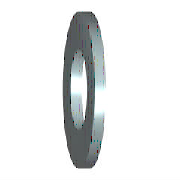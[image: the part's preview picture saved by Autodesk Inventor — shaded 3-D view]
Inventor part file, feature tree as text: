
AUTODESK INVENTOR PART (.ipt)
format: ipt  version: 2015 (Build 190159000, 159)  size: 105,984 bytes
history: native  units: mm (DEFAULTED — no unit token found)
features: other x1, plane x1, sketch x1
ambient origin geometry x7: Origin, YZ Plane, XY Plane, X Axis, Y Axis, Z Axis, Center Point
bodies: Solid1 (feature_tree), Body (feature_tree)
feature tree (3):
  other  "Work Axis1"
  plane  "Work Plane1"
  sketch  "Sketch"  dims[d0=10.5mm d1=20.0mm d2=2.0mm d3=0.0mm d4=0.0mm d5=0.0mm d6=0.0mm d7=0.0mm]
